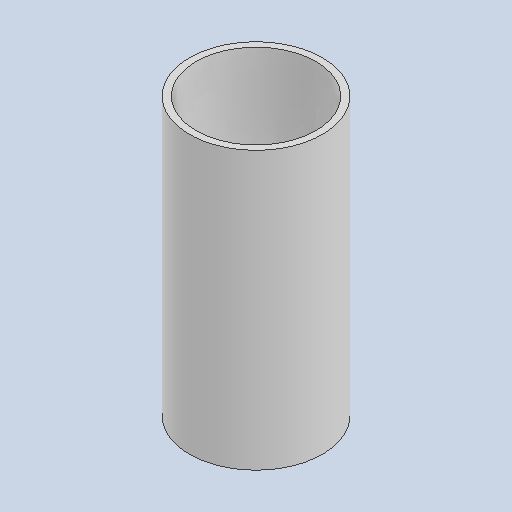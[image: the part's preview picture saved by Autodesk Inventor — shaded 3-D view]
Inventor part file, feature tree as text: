
AUTODESK INVENTOR PART (.ipt)
format: ipt  version: 2022 (Build 260153000, 153)  size: 97,280 bytes
history: native  units: in
note: dims shown in document units (in); Inventor stores cm internally (conversion verified against a paired STEP export)
features: shell x1
ambient origin geometry x8: Origin, YZ Plane, XZ Plane, XY Plane, X Axis, Y Axis, Z Axis, Center Point
bodies: Solid1 (feature_tree)
feature tree (1):
  shell  "Shell1"  [1 undecoded]
note: 1 required parameter value undecoded (feature->parameter linkage not recoverable at this tier; creation-order binding heuristic only, values carry confidence <= 0.55)
